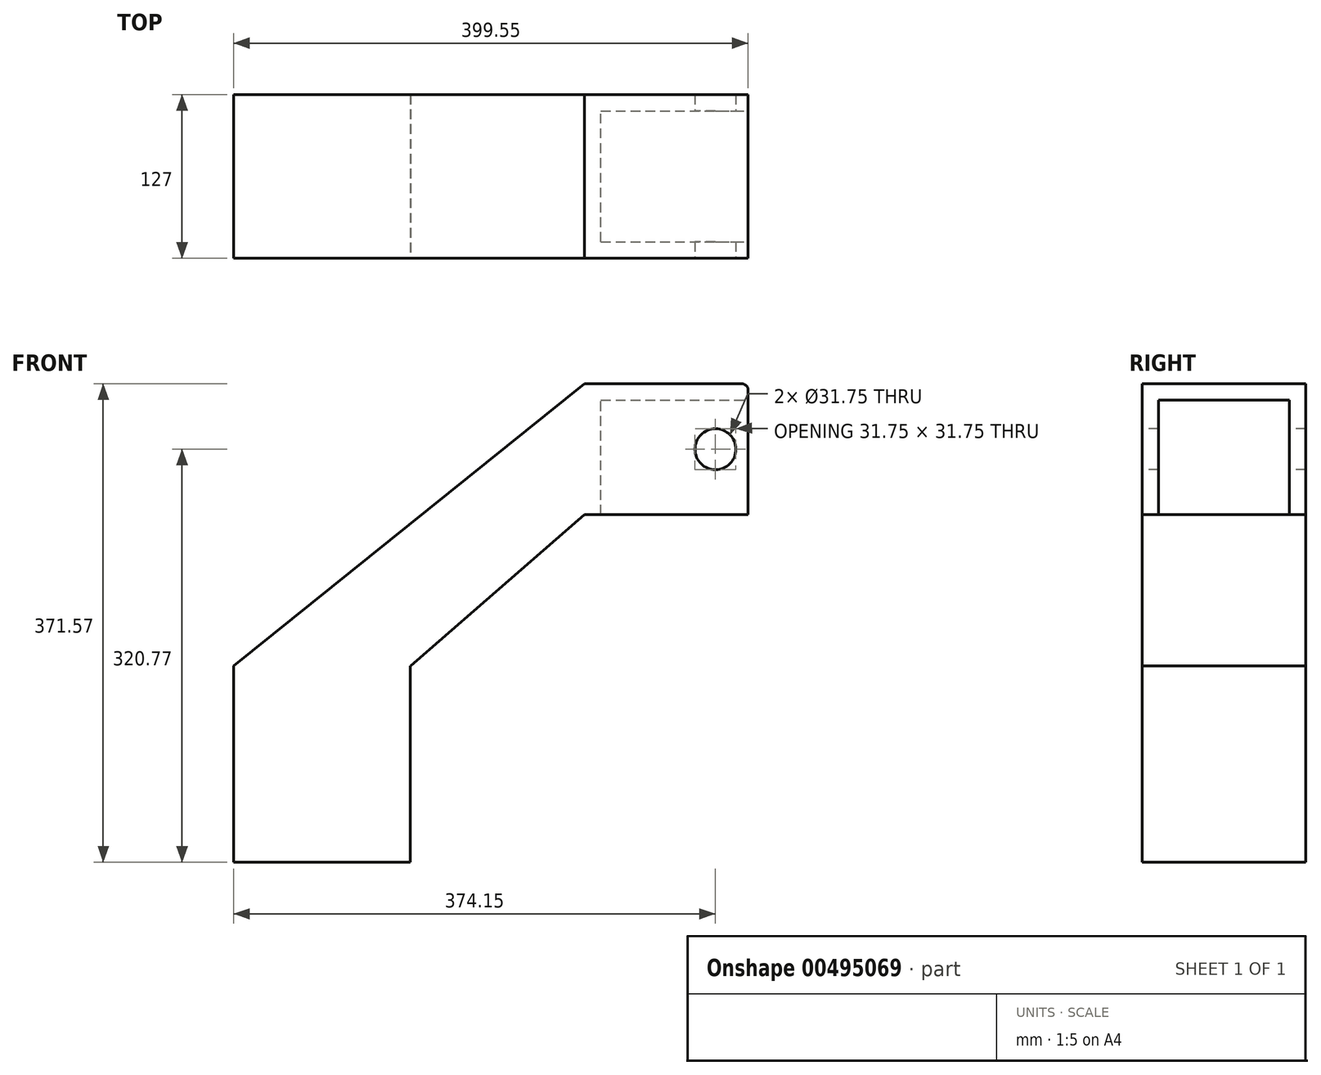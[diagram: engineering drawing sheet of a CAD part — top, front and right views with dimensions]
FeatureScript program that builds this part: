
annotation { "Feature Type Name" : "Feature", "Feature Type Description" : "" }
export const myFeature = defineFeature(function(context is Context, id is Id, definition is map)
    precondition{}
    {
        {
            var Q0;
            Q0=qCreatedBy(makeId("Top.planeOp"),FACE);
            var sketch = newSketch(context, id + "F0", { "sketchPlane" : qUnion([Q0])});
            skLineSegment(sketch, "E0.bottom", {"start": v(0, 0) * mm, "end": v(127, 0) * mm});
            skLineSegment(sketch, "E0.top", {"start": v(0, 127) * mm, "end": v(127, 127) * mm});
            skLineSegment(sketch, "E0.left", {"start": v(0, 0) * mm, "end": v(0, 127) * mm});
            skLineSegment(sketch, "E0.right", {"start": v(127, 0) * mm, "end": v(127, 127) * mm});
            skSolve(sketch);
        }
        {
            var Q0;
            Q0=makeQuery(id+"F0.imprint","IMPRINT",FACE,{"disambiguationData":[TD([[makeQuery(id+"F0.imprint","IMPRINT",EDGE,{"derivedFrom":sQuery(id+"F0.wireOp",EDGE,"E0.bottom")}),1.0]])]});
            extrude(context, id + "F1", {"entities" : qUnion([Q0]), "oppositeDirection" : true, "depth" : 101.6 * mm});
        }
        {
            var Q0;
            Q0=makeQuery(id+"F1.opExtrude","SWEPT_FACE",FACE,{"disambiguationData":[OSD([sQuery(id+"F0.wireOp",EDGE,"E0.right")])]});
            var sketch = newSketch(context, id + "F2", { "sketchPlane" : qUnion([Q0])});
            skLineSegment(sketch, "E1.bottom", {"start": v(12.7, -101.6) * mm, "end": v(114.3, -101.6) * mm});
            skLineSegment(sketch, "E1.top", {"start": v(12.7, -12.7) * mm, "end": v(114.3, -12.7) * mm});
            skLineSegment(sketch, "E1.left", {"start": v(12.7, -101.6) * mm, "end": v(12.7, -12.7) * mm});
            skLineSegment(sketch, "E1.right", {"start": v(114.3, -101.6) * mm, "end": v(114.3, -12.7) * mm});
            skSolve(sketch);
        }
        {
            var Q0;
            Q0 = qSketchRegion(id + "F2", true);
            extrude(context, id + "F3", {"entities" : qUnion([Q0]), "operationType" : NewBodyOperationType.REMOVE, "oppositeDirection" : true, "depth" : 114.3 * mm});
        }
        {
            var Q0;
            Q0=makeQuery(id+"F1.opExtrude","SWEPT_FACE",FACE,{"disambiguationData":[OSD([sQuery(id+"F0.wireOp",EDGE,"E0.bottom")])]});
            var sketch = newSketch(context, id + "F4", { "sketchPlane" : qUnion([Q0])});
            skCircle(sketch, "E2", {"center": v(101.6, -50.8) * mm, "radius": 15.88 * mm});
            skSolve(sketch);
        }
        {
            var Q0;
            Q0=makeQuery(id+"F4.imprint","IMPRINT",FACE,{"disambiguationData":[TD([[makeQuery(id+"F4.imprint","IMPRINT",EDGE,{"derivedFrom":sQuery(id+"F4.wireOp",EDGE,"E2")}),1.0]])]});
            extrude(context, id + "F5", {"entities" : qUnion([Q0]), "operationType" : NewBodyOperationType.REMOVE, "endBound" : BoundingType.THROUGH_ALL, "oppositeDirection" : true, "depth" : 25.4 * mm});
        }
        {
            var Q0;
            Q0=makeQuery(id+"F1.opExtrude","CAP_EDGE",EDGE,{"disambiguationData":[OSD([sQuery(id+"F0.wireOp",EDGE,"E0.right")])],"isStart":true});
            fillet(context, id + "F6", {"entities" : qUnion([Q0]), "radius" : 5.08 * mm, "tangentPropagation" : true, "allowEdgeOverflow" : false});
        }
        {
            var Q0;
            Q0=makeQuery(id+"F1.opExtrude","SWEPT_FACE",FACE,{"disambiguationData":[OSD([sQuery(id+"F0.wireOp",EDGE,"E0.bottom")])]});
            var sketch = newSketch(context, id + "F7", { "sketchPlane" : qUnion([Q0])});
            skLineSegment(sketch, "E3", {"start": v(0, 0) * mm, "end": v(-272.55, -219.17) * mm});
            skLineSegment(sketch, "E4", {"start": v(-272.55, -219.17) * mm, "end": v(-135.08, -219.17) * mm});
            skLineSegment(sketch, "E5", {"start": v(-135.08, -219.17) * mm, "end": v(0, -101.6) * mm});
            skSolve(sketch);
        }
        {
            var Q0;
            Q0 = qSketchRegion(id + "F7", true);
            var Q1;
            Q1=makeQuery(id+"F7.imprint","IMPRINT",FACE,{"disambiguationData":[TD([[makeQuery(id+"F7.imprint","IMPRINT",EDGE,{"derivedFrom":sQuery(id+"F7.wireOp",EDGE,"E3")}),1.0]])]});
            extrude(context, id + "F8", {"entities" : qUnion([Q0, Q1]), "operationType" : NewBodyOperationType.ADD, "oppositeDirection" : true, "depth" : 127 * mm});
        }
        {
            var Q0;
            {var subQ0=sQuery(id+"F0.wireOp",EDGE,"E0.bottom");Q0=makeQuery(id+"F8.boolean.opBoolean","MERGE",FACE,{"derivedFrom":[makeQuery(id+"F1.opExtrude","SWEPT_FACE",FACE,{"disambiguationData":[OSD([subQ0])]}),makeQuery(id+"F8.opExtrude","CAP_FACE",FACE,{"disambiguationData":[OSD([subQ0,sQuery(id+"F0.wireOp",EDGE,"E0.left"),sQuery(id+"F7.wireOp",EDGE,"E3"),sQuery(id+"F7.wireOp",EDGE,"E4"),sQuery(id+"F7.wireOp",EDGE,"E5")])],"isStart":true})]});}
            var sketch = newSketch(context, id + "F9", { "sketchPlane" : qUnion([Q0])});
            skLineSegment(sketch, "E6.bottom", {"start": v(-272.55, -219.17) * mm, "end": v(-135.3, -219.17) * mm});
            skLineSegment(sketch, "E6.top", {"start": v(-272.55, -371.57) * mm, "end": v(-135.3, -371.57) * mm});
            skLineSegment(sketch, "E6.left", {"start": v(-272.55, -219.17) * mm, "end": v(-272.55, -371.57) * mm});
            skLineSegment(sketch, "E6.right", {"start": v(-135.3, -219.17) * mm, "end": v(-135.3, -371.57) * mm});
            skSolve(sketch);
        }
        {
            var Q0;
            Q0=makeQuery(id+"F9.imprint","IMPRINT",FACE,{"disambiguationData":[TD([[makeQuery(id+"F9.imprint","IMPRINT",EDGE,{"derivedFrom":sQuery(id+"F9.wireOp",EDGE,"E6.bottom")}),-1.0]])]});
            extrude(context, id + "F10", {"entities" : qUnion([Q0]), "operationType" : NewBodyOperationType.ADD, "oppositeDirection" : true, "depth" : 127 * mm});
        }
    });
